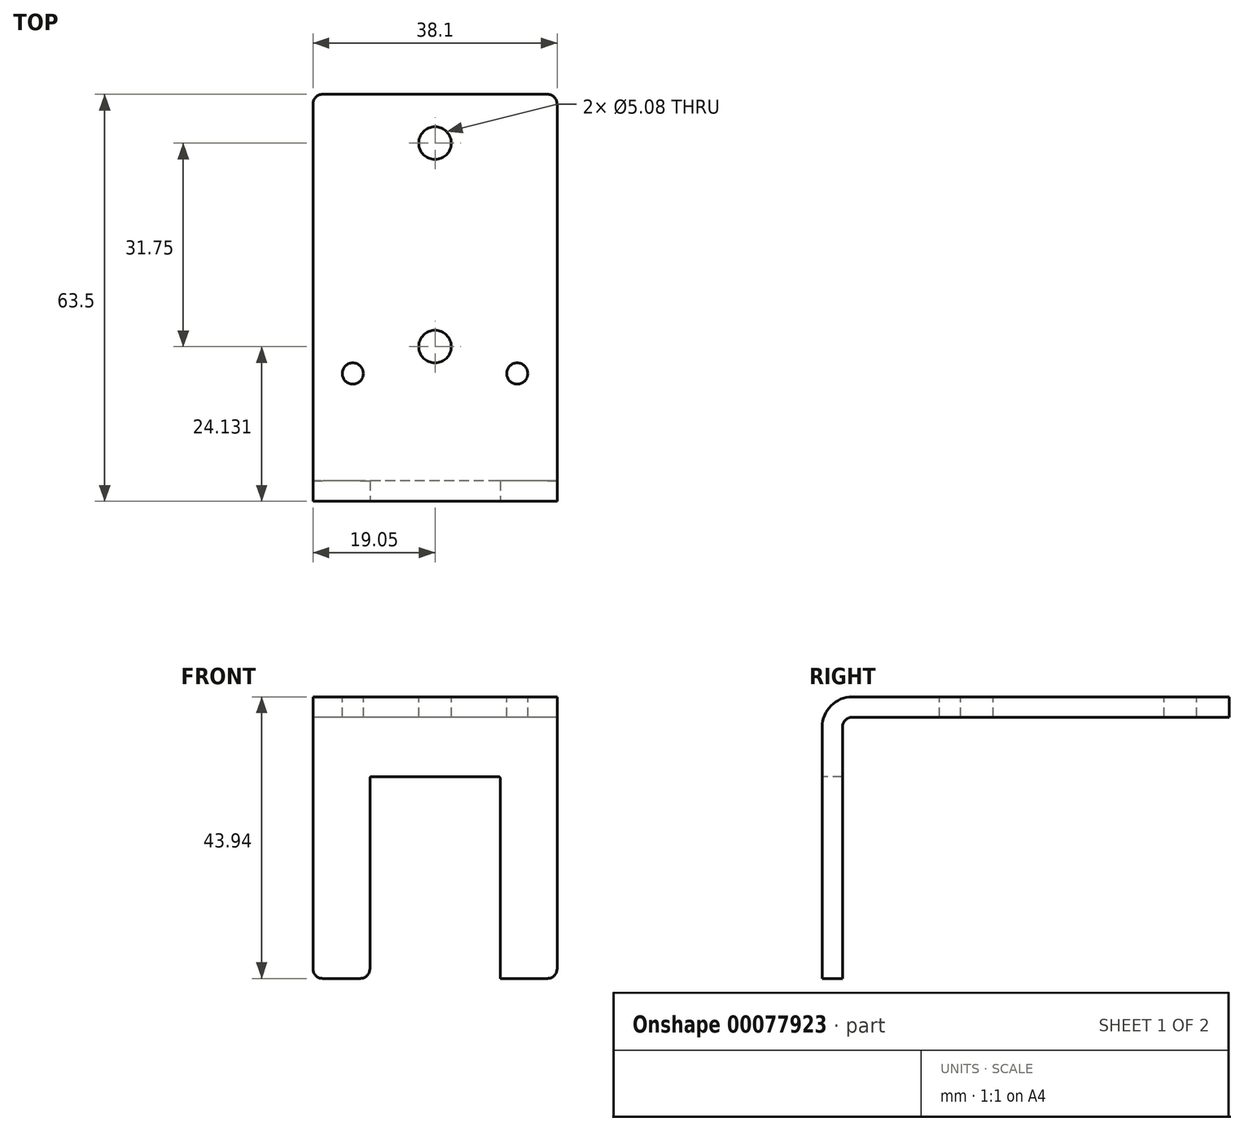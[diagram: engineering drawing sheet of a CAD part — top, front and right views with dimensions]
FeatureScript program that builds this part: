
annotation { "Feature Type Name" : "Feature", "Feature Type Description" : "" }
export const myFeature = defineFeature(function(context is Context, id is Id, definition is map)
    precondition{}
    {
        {
            var Q0;
            Q0=qCreatedBy(makeId("Right.planeOp"),FACE);
            var sketch = newSketch(context, id + "F0", { "sketchPlane" : qUnion([Q0])});
            skLineSegment(sketch, "E0.bottom", {"start": v(-60.85, 0) * mm, "end": v(-64.03, 0) * mm});
            skLineSegment(sketch, "E0.top", {"start": v(-0.53, 43.94) * mm, "end": v(-59.33, 43.94) * mm});
            skLineSegment(sketch, "E0.left", {"start": v(-0.53, 40.77) * mm, "end": v(-0.53, 43.94) * mm});
            skLineSegment(sketch, "E0.right", {"start": v(-64.03, 0) * mm, "end": v(-64.03, 39.24) * mm});
            skLineSegment(sketch, "E1", {"start": v(-60.85, 0) * mm, "end": v(-60.85, 39.24) * mm});
            skLineSegment(sketch, "E2", {"start": v(-59.33, 40.77) * mm, "end": v(-0.53, 40.77) * mm});
            skPoint(sketch, "E3.visualSharp", {"position": v(-60.85, 40.77) * mm});
            skArc(sketch, "E3.filletArc", {"start": v(-59.33, 40.77) * mm, "mid": v(-60.4, 40.32) * mm, "end": v(-60.85, 39.24) * mm});
            skPoint(sketch, "E4.visualSharp", {"position": v(-64.03, 43.94) * mm});
            skArc(sketch, "E4.filletArc", {"start": v(-59.33, 43.94) * mm, "mid": v(-62.65, 42.57) * mm, "end": v(-64.03, 39.24) * mm});
            skSolve(sketch);
        }
        {
            var Q0;
            Q0 = qSketchRegion(id + "F0", true);
            extrude(context, id + "F1", {"entities" : qUnion([Q0]), "depth" : 38.1 * mm});
        }
        {
            var Q0;
            Q0=makeQuery(id+"F1.opExtrude","SWEPT_FACE",FACE,{"disambiguationData":[OSD([sQuery(id+"F0.wireOp",EDGE,"E0.right")])]});
            var sketch = newSketch(context, id + "F2", { "sketchPlane" : qUnion([Q0])});
            skLineSegment(sketch, "E5.bottom", {"start": v(8.9, 0) * mm, "end": v(29.21, 0) * mm});
            skLineSegment(sketch, "E5.top", {"start": v(9.14, 31.5) * mm, "end": v(28.96, 31.5) * mm});
            skLineSegment(sketch, "E5.left", {"start": v(8.9, 0) * mm, "end": v(8.9, 31.24) * mm});
            skLineSegment(sketch, "E5.right", {"start": v(29.21, 0) * mm, "end": v(29.21, 31.24) * mm});
            skPoint(sketch, "E6.visualSharp", {"position": v(8.9, 31.5) * mm});
            skArc(sketch, "E6.filletArc", {"start": v(9.14, 31.5) * mm, "mid": v(8.96, 31.42) * mm, "end": v(8.9, 31.24) * mm});
            skPoint(sketch, "E7.visualSharp", {"position": v(29.21, 31.5) * mm});
            skArc(sketch, "E7.filletArc", {"start": v(29.21, 31.24) * mm, "mid": v(29.14, 31.42) * mm, "end": v(28.96, 31.5) * mm});
            skSolve(sketch);
        }
        {
            var Q0;
            Q0 = qSketchRegion(id + "F2", true);
            extrude(context, id + "F3", {"entities" : qUnion([Q0]), "operationType" : NewBodyOperationType.REMOVE, "endBound" : BoundingType.UP_TO_NEXT, "oppositeDirection" : true, "depth" : 25.4 * mm});
        }
        {
            var Q0;
            Q0=makeQuery(id+"F3.boolean.opBoolean","COPY",EDGE,{"derivedFrom":makeQuery(id+"F3.opExtrude","SWEPT_EDGE",EDGE,{"disambiguationData":[OSD([sQuery(id+"F0.wireOp",EDGE,"E0.bottom"),sQuery(id+"F0.wireOp",EDGE,"E0.right"),sQuery(id+"F2.wireOp",EDGE,"E5.bottom"),sQuery(id+"F2.wireOp",EDGE,"E5.left")])]})});
            var Q1;
            Q1=makeQuery(id+"F1.opExtrude","CAP_EDGE",EDGE,{"disambiguationData":[OSD([sQuery(id+"F0.wireOp",EDGE,"E0.bottom")])],"isStart":true});
            var Q2;
            Q2=makeQuery(id+"F3.boolean.opBoolean","COPY",EDGE,{"derivedFrom":makeQuery(id+"F3.opExtrude","SWEPT_EDGE",EDGE,{"disambiguationData":[OSD([sQuery(id+"F0.wireOp",EDGE,"E0.bottom"),sQuery(id+"F0.wireOp",EDGE,"E0.right"),sQuery(id+"F2.wireOp",EDGE,"E5.bottom"),sQuery(id+"F2.wireOp",EDGE,"E5.right")])]})});
            var Q3;
            Q3=makeQuery(id+"F1.opExtrude","CAP_EDGE",EDGE,{"disambiguationData":[OSD([sQuery(id+"F0.wireOp",EDGE,"E0.bottom")])],"isStart":false});
            var Q4;
            Q4=makeQuery(id+"F1.opExtrude","CAP_EDGE",EDGE,{"disambiguationData":[OSD([sQuery(id+"F0.wireOp",EDGE,"E0.left")])],"isStart":false});
            var Q5;
            Q5=makeQuery(id+"F1.opExtrude","CAP_EDGE",EDGE,{"disambiguationData":[OSD([sQuery(id+"F0.wireOp",EDGE,"E0.left")])],"isStart":true});
            fillet(context, id + "F4", {"entities" : qUnion([Q0, Q1, Q2, Q3, Q4, Q5]), "radius" : 1.52 * mm, "tangentPropagation" : true, "allowEdgeOverflow" : false});
        }
        {
            var Q0;
            Q0=makeQuery(id+"F1.opExtrude","SWEPT_FACE",FACE,{"disambiguationData":[OSD([sQuery(id+"F0.wireOp",EDGE,"E0.top")])]});
            var sketch = newSketch(context, id + "F5", { "sketchPlane" : qUnion([Q0])});
            skLineSegment(sketch, "E8", {"start": v(19.05, -0.53) * mm, "end": v(19.05, -59.33) * mm, "construction": true});
            skLineSegment(sketch, "E9", {"start": v(38.1, -44.1) * mm, "end": v(0, -44.1) * mm, "construction": true});
            skCircle(sketch, "E10", {"center": v(19.05, -8.15) * mm, "radius": 2.54 * mm});
            skCircle(sketch, "E11", {"center": v(19.05, -39.9) * mm, "radius": 2.54 * mm});
            skCircle(sketch, "E12", {"center": v(31.88, -44.1) * mm, "radius": 1.65 * mm});
            skCircle(sketch, "E13", {"center": v(6.22, -44.1) * mm, "radius": 1.65 * mm});
            skSolve(sketch);
        }
        {
            var Q0;
            Q0 = qSketchRegion(id + "F5", true);
            extrude(context, id + "F6", {"entities" : qUnion([Q0]), "operationType" : NewBodyOperationType.REMOVE, "endBound" : BoundingType.UP_TO_NEXT, "oppositeDirection" : true, "depth" : 25.4 * mm});
        }
    });
